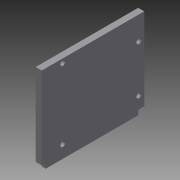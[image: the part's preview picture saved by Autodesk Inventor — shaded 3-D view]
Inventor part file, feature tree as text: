
AUTODESK INVENTOR PART (.ipt)
format: ipt  version: 2015 SP2 (Build 190223200, 223)  size: 100,864 bytes
history: native  units: in
note: dims shown in document units (in); Inventor stores cm internally (conversion verified against a paired STEP export)
features: sketch x3, extrude x2, plane x1, hole x1
ambient origin geometry x8: Origin, YZ Plane, XZ Plane, XY Plane, X Axis, Y Axis, Z Axis, Center Point
bodies: Solid1 (feature_tree)
feature tree (7):
  plane  "Work Plane1"
  extrude  "Extrusion1"  Depth=0.1063in
  extrude  "Extrusion2"  Depth=0.1575in TaperAngle=0.0deg
  hole  "Hole2"  [1 undecoded]
  sketch  "Sketch1"  dims[d0=2.2047in d1=0.0in d14=0.1063in]
  sketch  "Sketch3"  dims[d15=2.4803in d16=0.1575in d17=0.0in]
  sketch  "Sketch4"  dims[d20=0.126in d22=0.126in d23=2.0394in d24=0.1092in d25=0.126in d27=0.126in d28=0.126in d29=0.2362in d30=0.1575in d31=0.0787in d32=90.0deg d33=0.315in d34=0.8108in]
note: 1 required parameter value undecoded (feature->parameter linkage not recoverable at this tier; creation-order binding heuristic only, values carry confidence <= 0.55)
